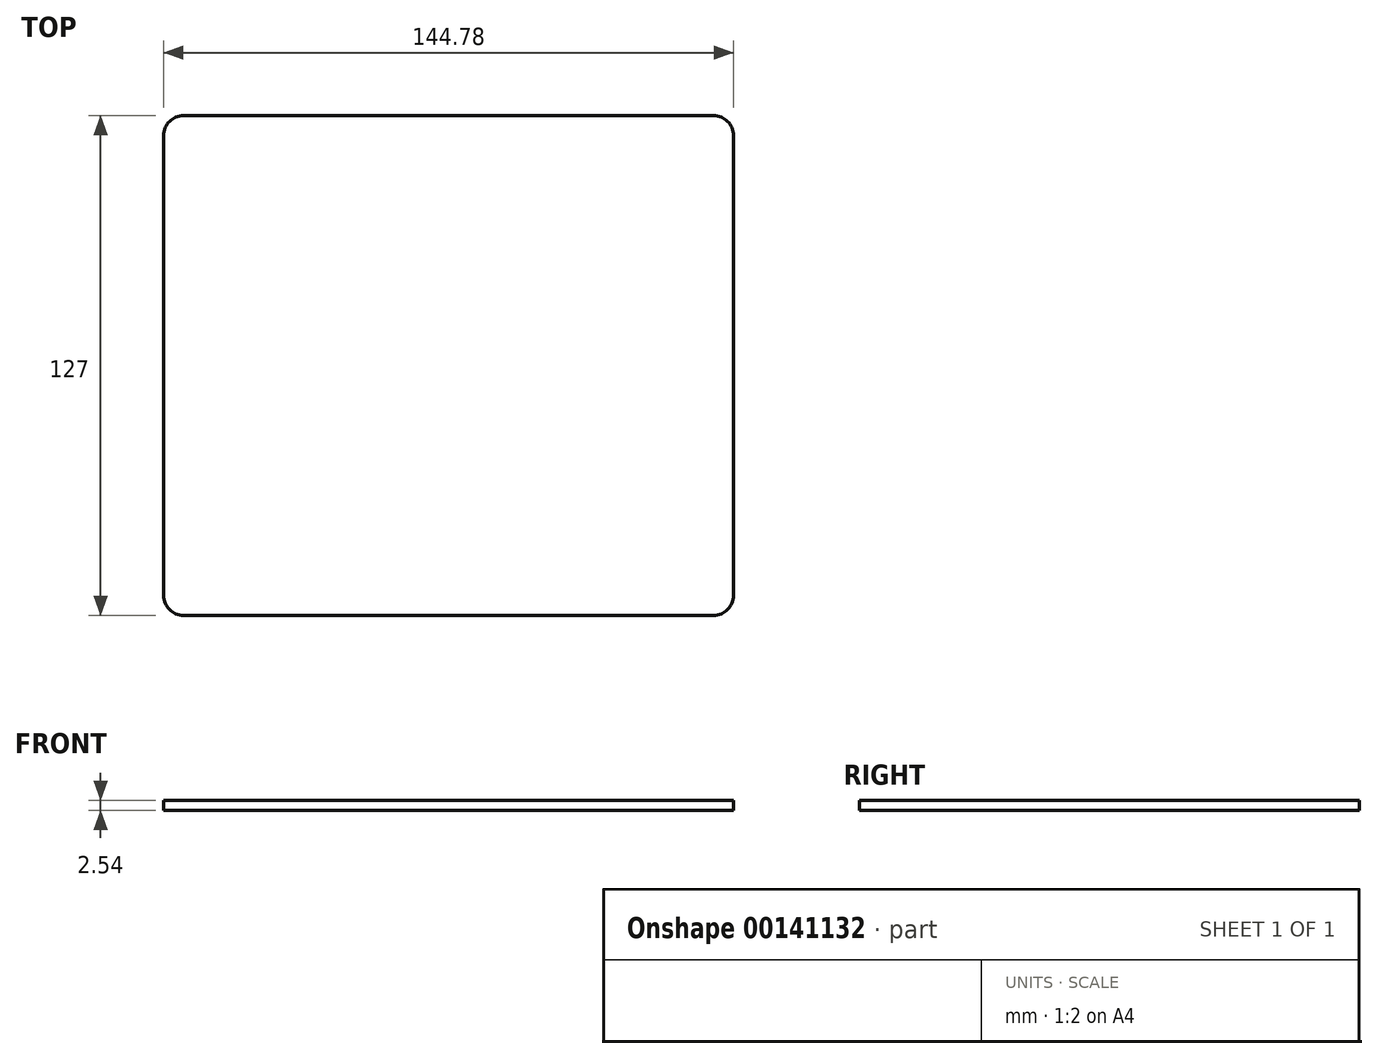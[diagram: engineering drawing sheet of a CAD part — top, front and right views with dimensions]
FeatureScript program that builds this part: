
annotation { "Feature Type Name" : "Feature", "Feature Type Description" : "" }
export const myFeature = defineFeature(function(context is Context, id is Id, definition is map)
    precondition{}
    {
        {
            var Q0;
            Q0=qCreatedBy(makeId("Top.planeOp"),FACE);
            var sketch = newSketch(context, id + "F0", { "sketchPlane" : qUnion([Q0])});
            skLineSegment(sketch, "E0.bottom", {"start": v(48, -37.1) * mm, "end": v(-91.7, -37.1) * mm});
            skLineSegment(sketch, "E0.top", {"start": v(48, 84.82) * mm, "end": v(-91.7, 84.82) * mm});
            skLineSegment(sketch, "E0.left", {"start": v(48, -37.1) * mm, "end": v(48, 84.82) * mm});
            skLineSegment(sketch, "E0.right", {"start": v(-91.7, -37.1) * mm, "end": v(-91.7, 84.82) * mm});
            skPoint(sketch, "E0.middle", {"position": v(-21.85, 23.86) * mm});
            skSolve(sketch);
        }
        {
            var Q0;
            Q0=qSketchRegion(id+"F0",true);
            extrude(context, id + "F1", {"entities" : qUnion([Q0]), "depth" : 2.54 * mm});
        }
        {
            var Q0;
            Q0=makeQuery(id+"F1.opExtrude","SWEPT_BODY",BODY,{"disambiguationData":[OSD([sQuery(id+"F0.wireOp",EDGE,"E0.bottom"),sQuery(id+"F0.wireOp",EDGE,"E0.top"),sQuery(id+"F0.wireOp",EDGE,"E0.left"),sQuery(id+"F0.wireOp",EDGE,"E0.right")])]});
            deleteBodies(context, id + "F2", {"entities" : qUnion([Q0])});
        }
        {
            var Q0;
            Q0=qCreatedBy(makeId("Top.planeOp"),FACE);
            var sketch = newSketch(context, id + "F3", { "sketchPlane" : qUnion([Q0])});
            skLineSegment(sketch, "E1.bottom", {"start": v(72.4, 63.5) * mm, "end": v(-72.4, 63.5) * mm});
            skLineSegment(sketch, "E1.top", {"start": v(72.4, -63.5) * mm, "end": v(-72.4, -63.5) * mm});
            skLineSegment(sketch, "E1.left", {"start": v(72.4, 63.5) * mm, "end": v(72.4, -63.5) * mm});
            skLineSegment(sketch, "E1.right", {"start": v(-72.4, 63.5) * mm, "end": v(-72.4, -63.5) * mm});
            skPoint(sketch, "E1.middle", {"position": v(0, 0) * mm});
            skSolve(sketch);
        }
        {
            var Q0;
            Q0=makeQuery(id+"F3.imprint","IMPRINT",FACE,{"disambiguationData":[TD([[makeQuery(id+"F3.imprint","IMPRINT",EDGE,{"derivedFrom":sQuery(id+"F3.wireOp",EDGE,"E1.bottom")}),1.0]])]});
            extrude(context, id + "F4", {"entities" : qUnion([Q0]), "depth" : 2.54 * mm});
        }
        {
            var Q0;
            Q0=makeQuery(id+"F4.opExtrude","SWEPT_EDGE",EDGE,{"disambiguationData":[OSD([sQuery(id+"F3.wireOp",EDGE,"E1.bottom"),sQuery(id+"F3.wireOp",EDGE,"E1.right")])]});
            var Q1;
            Q1=makeQuery(id+"F4.opExtrude","SWEPT_EDGE",EDGE,{"disambiguationData":[OSD([sQuery(id+"F3.wireOp",EDGE,"E1.bottom"),sQuery(id+"F3.wireOp",EDGE,"E1.left")])]});
            var Q2;
            Q2=makeQuery(id+"F4.opExtrude","SWEPT_EDGE",EDGE,{"disambiguationData":[OSD([sQuery(id+"F3.wireOp",EDGE,"E1.top"),sQuery(id+"F3.wireOp",EDGE,"E1.left")])]});
            var Q3;
            Q3=makeQuery(id+"F4.opExtrude","SWEPT_EDGE",EDGE,{"disambiguationData":[OSD([sQuery(id+"F3.wireOp",EDGE,"E1.top"),sQuery(id+"F3.wireOp",EDGE,"E1.right")])]});
            fillet(context, id + "F5", {"entities" : qUnion([Q0, Q1, Q2, Q3]), "radius" : 5.08 * mm, "tangentPropagation" : true, "allowEdgeOverflow" : false});
        }
    });
